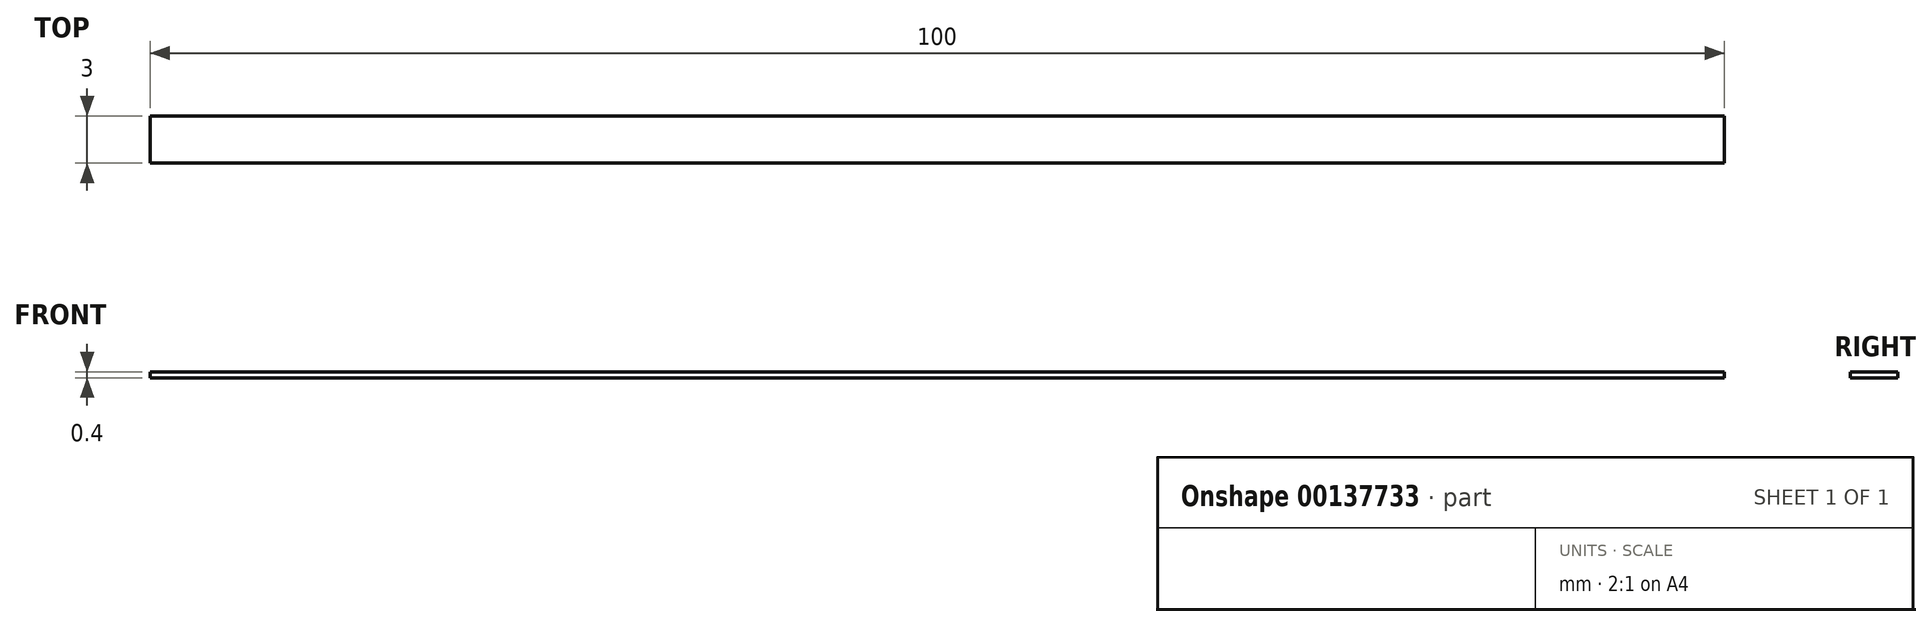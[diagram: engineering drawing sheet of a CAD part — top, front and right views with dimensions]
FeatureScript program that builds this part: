
annotation { "Feature Type Name" : "Feature", "Feature Type Description" : "" }
export const myFeature = defineFeature(function(context is Context, id is Id, definition is map)
    precondition{}
    {
        {
            var Q0;
            Q0=qCreatedBy(makeId("Top.planeOp"),FACE);
            var sketch = newSketch(context, id + "F0", { "sketchPlane" : qUnion([Q0])});
            skLineSegment(sketch, "E0", {"start": v(-44.73, 0) * mm, "end": v(55.27, 0) * mm});
            skLineSegment(sketch, "E1", {"start": v(55.27, 0) * mm, "end": v(55.27, 3) * mm});
            skLineSegment(sketch, "E2", {"start": v(55.27, 3) * mm, "end": v(-44.73, 3) * mm});
            skLineSegment(sketch, "E3", {"start": v(-44.73, 3) * mm, "end": v(-44.73, 0) * mm});
            skSolve(sketch);
        }
        {
            var Q0;
            Q0 = qSketchRegion(id + "F0", true);
            extrude(context, id + "F1", {"entities" : qUnion([Q0]), "depth" : .4 * mm});
        }
    });
